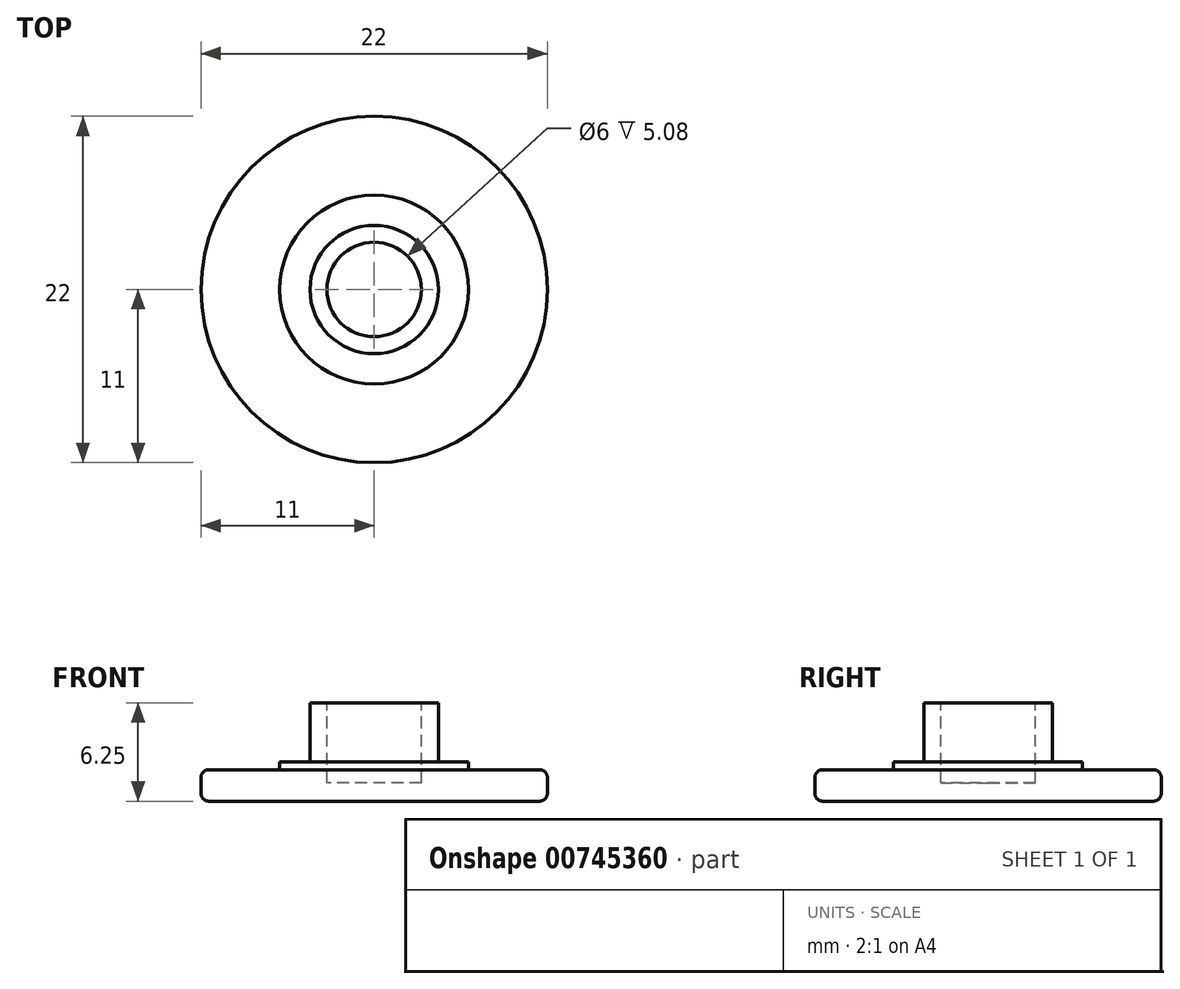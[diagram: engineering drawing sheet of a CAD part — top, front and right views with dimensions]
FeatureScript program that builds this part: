
annotation { "Feature Type Name" : "Feature", "Feature Type Description" : "" }
export const myFeature = defineFeature(function(context is Context, id is Id, definition is map)
    precondition{}
    {
        {
            var Q0;
            Q0=qCreatedBy(makeId("Top.planeOp"),FACE);
            var sketch = newSketch(context, id + "F0", { "sketchPlane" : qUnion([Q0])});
            skCircle(sketch, "E0", {"center": v(0, 0) * mm, "radius": 11 * mm});
            skSolve(sketch);
        }
        {
            var Q0;
            Q0=qSketchRegion(id+"F0",true);
            extrude(context, id + "F1", {"entities" : qUnion([Q0]), "depth" : 2 * mm, "offsetDistance" : 25 * mm});
        }
        {
            var Q0;
            Q0=makeQuery(id+"F1.opExtrude","CAP_FACE",FACE,{"disambiguationData":[OSD([sQuery(id+"F0.wireOp",EDGE,"E0")])],"isStart":false});
            var sketch = newSketch(context, id + "F2", { "sketchPlane" : qUnion([Q0])});
            skCircle(sketch, "E1", {"center": v(0, 0) * mm, "radius": 6 * mm});
            skSolve(sketch);
        }
        {
            var Q0;
            Q0=qSketchRegion(id+"F2",true);
            extrude(context, id + "F3", {"entities" : qUnion([Q0]), "operationType" : NewBodyOperationType.ADD, "depth" : 0.5 * mm, "offsetDistance" : 25 * mm});
        }
        {
            var Q0;
            Q0=makeQuery(id+"F3.opExtrude","CAP_FACE",FACE,{"disambiguationData":[OSD([sQuery(id+"F2.wireOp",EDGE,"E1")])],"isStart":false});
            var sketch = newSketch(context, id + "F4", { "sketchPlane" : qUnion([Q0])});
            skCircle(sketch, "E2", {"center": v(0, 0) * mm, "radius": 4.08 * mm});
            skSolve(sketch);
        }
        {
            var Q0;
            Q0=qSketchRegion(id+"F4",true);
            extrude(context, id + "F5", {"entities" : qUnion([Q0]), "operationType" : NewBodyOperationType.ADD, "depth" : (7.5 / 2) * mm, "offsetDistance" : 25 * mm});
        }
        {
            var Q0;
            Q0=makeQuery(id+"F5.opExtrude","CAP_FACE",FACE,{"disambiguationData":[OSD([sQuery(id+"F4.wireOp",EDGE,"E2")])],"isStart":false});
            var sketch = newSketch(context, id + "F6", { "sketchPlane" : qUnion([Q0])});
            skCircle(sketch, "E3", {"center": v(0, 0) * mm, "radius": 3 * mm});
            skSolve(sketch);
        }
        {
            var Q0;
            Q0=qSketchRegion(id+"F6",true);
            extrude(context, id + "F7", {"entities" : qUnion([Q0]), "operationType" : NewBodyOperationType.REMOVE, "oppositeDirection" : true, "depth" : 5.08 * mm, "offsetDistance" : 25 * mm});
        }
        {
            var Q0;
            Q0=makeQuery(id+"F1.opExtrude","CAP_EDGE",EDGE,{"disambiguationData":[OSD([sQuery(id+"F0.wireOp",EDGE,"E0")])],"isStart":false});
            var Q1;
            Q1=makeQuery(id+"F1.opExtrude","CAP_EDGE",EDGE,{"disambiguationData":[OSD([sQuery(id+"F0.wireOp",EDGE,"E0")])],"isStart":true});
            fillet(context, id + "F8", {"entities" : qUnion([Q0, Q1]), "radius" : 0.5 * mm, "tangentPropagation" : true, "allowEdgeOverflow" : false});
        }
    });
